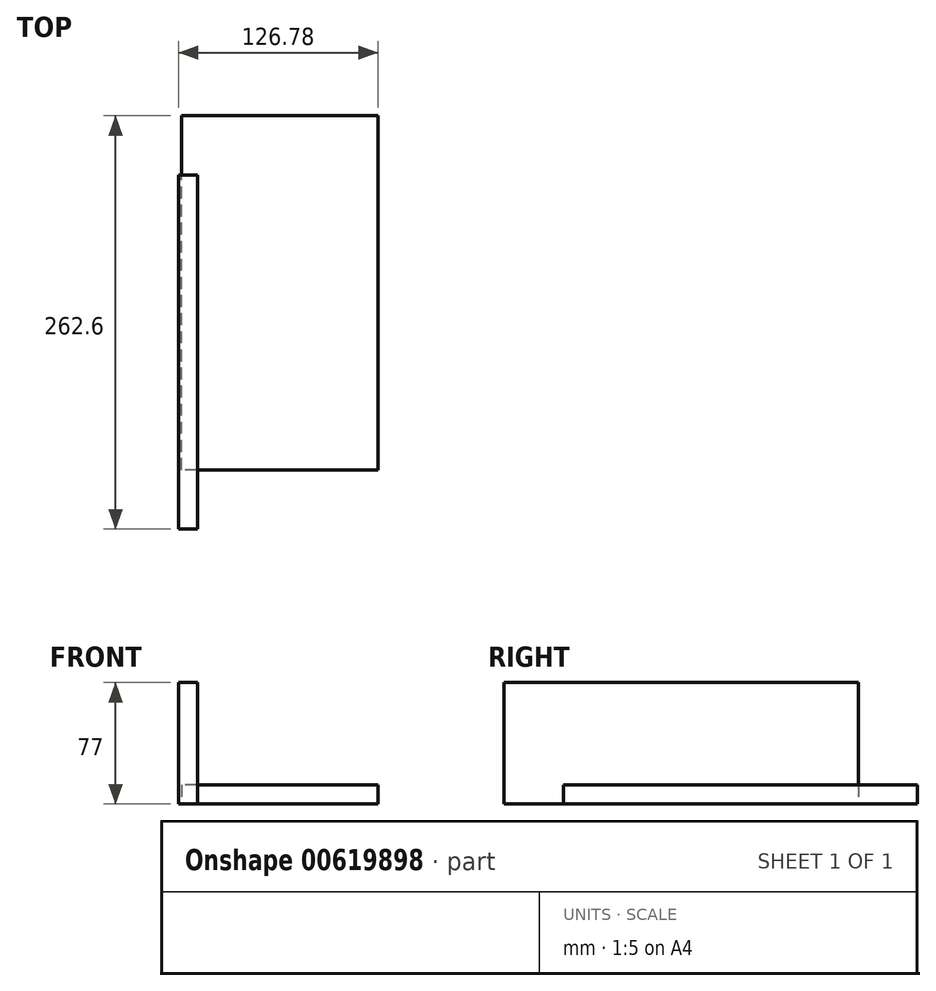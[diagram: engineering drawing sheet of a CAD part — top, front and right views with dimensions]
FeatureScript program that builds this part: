
annotation { "Feature Type Name" : "Feature", "Feature Type Description" : "" }
export const myFeature = defineFeature(function(context is Context, id is Id, definition is map)
    precondition{}
    {
        {
            var Q0;
            Q0=qCreatedBy(makeId("Top.planeOp"),FACE);
            var sketch = newSketch(context, id + "F0", { "sketchPlane" : qUnion([Q0])});
            skLineSegment(sketch, "E0.bottom", {"start": v(62.5, -112.5) * mm, "end": v(-62.5, -112.5) * mm});
            skLineSegment(sketch, "E0.top", {"start": v(62.5, 112.5) * mm, "end": v(-62.5, 112.5) * mm});
            skLineSegment(sketch, "E0.left", {"start": v(62.5, -112.5) * mm, "end": v(62.5, 112.5) * mm});
            skLineSegment(sketch, "E0.right", {"start": v(-62.5, -112.5) * mm, "end": v(-62.5, 112.5) * mm});
            skPoint(sketch, "E0.middle", {"position": v(0, 0) * mm});
            skSolve(sketch);
        }
        {
            var Q0;
            Q0=makeQuery(id+"F0.imprint","IMPRINT",FACE,{"disambiguationData":[TD([[makeQuery(id+"F0.imprint","IMPRINT",EDGE,{"derivedFrom":sQuery(id+"F0.wireOp",EDGE,"E0.bottom")}),-1.0]])]});
            extrude(context, id + "F1", {"entities" : qUnion([Q0]), "depth" : 12 * mm, "offsetDistance" : 25 * mm});
        }
        {
            var Q0;
            Q0=qCreatedBy(makeId("Top.planeOp"),FACE);
            var sketch = newSketch(context, id + "F2", { "sketchPlane" : qUnion([Q0])});
            skLineSegment(sketch, "E1.bottom", {"start": v(-64.28, -150.1) * mm, "end": v(-52.28, -150.1) * mm});
            skLineSegment(sketch, "E1.top", {"start": v(-64.28, 74.9) * mm, "end": v(-52.28, 74.9) * mm});
            skLineSegment(sketch, "E1.left", {"start": v(-64.28, -150.1) * mm, "end": v(-64.28, 74.9) * mm});
            skLineSegment(sketch, "E1.right", {"start": v(-52.28, -150.1) * mm, "end": v(-52.28, 74.9) * mm});
            skSolve(sketch);
        }
        {
            var Q0;
            Q0=makeQuery(id+"F2.imprint","IMPRINT",FACE,{"disambiguationData":[TD([[makeQuery(id+"F2.imprint","IMPRINT",EDGE,{"derivedFrom":sQuery(id+"F2.wireOp",EDGE,"E1.bottom")}),1.0]])]});
            extrude(context, id + "F3", {"entities" : qUnion([Q0]), "depth" : 77 * mm, "offsetDistance" : 25 * mm});
        }
    });
